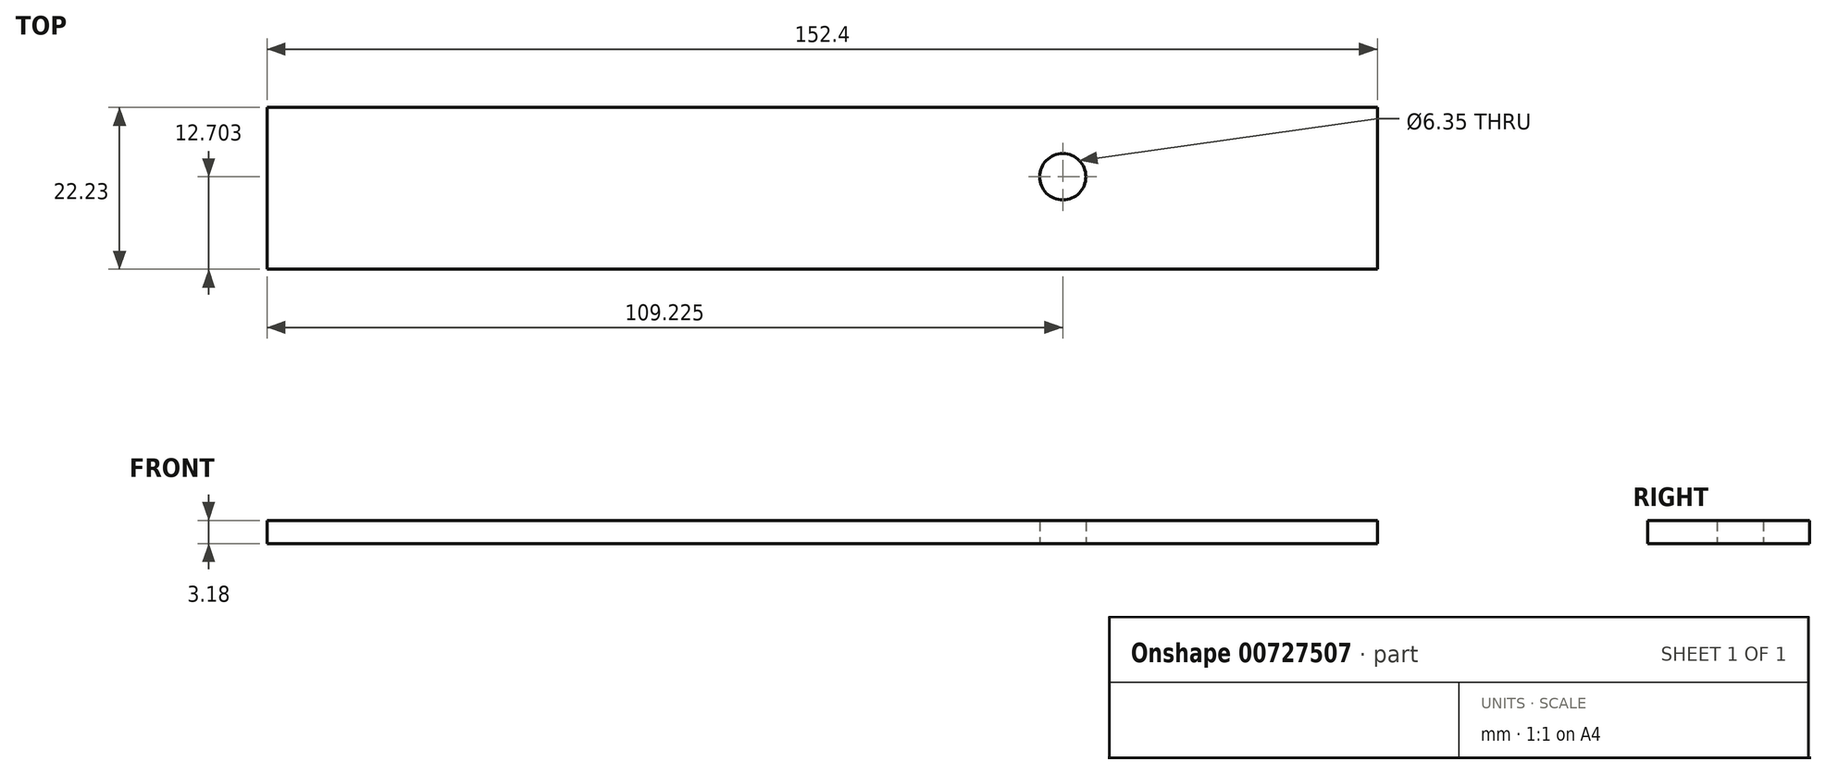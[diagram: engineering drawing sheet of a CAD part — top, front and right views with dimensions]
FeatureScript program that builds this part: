
annotation { "Feature Type Name" : "Feature", "Feature Type Description" : "" }
export const myFeature = defineFeature(function(context is Context, id is Id, definition is map)
    precondition{}
    {
        {
            var Q0;
            Q0=qCreatedBy(makeId("Top.planeOp"),FACE);
            var sketch = newSketch(context, id + "F0", { "sketchPlane" : qUnion([Q0])});
            skLineSegment(sketch, "E0.bottom", {"start": v(-83.24, 4.33) * mm, "end": v(69.16, 4.33) * mm});
            skLineSegment(sketch, "E0.top", {"start": v(-83.24, -17.9) * mm, "end": v(69.16, -17.9) * mm});
            skLineSegment(sketch, "E0.left", {"start": v(-83.24, 4.33) * mm, "end": v(-83.24, -17.9) * mm});
            skLineSegment(sketch, "E0.right", {"start": v(69.16, 4.33) * mm, "end": v(69.16, -17.9) * mm});
            skCircle(sketch, "E1", {"center": v(25.98, -5.2) * mm, "radius": 3.18 * mm});
            skSolve(sketch);
        }
        {
            var Q0;
            Q0 = qSketchRegion(id + "F0", true);
            extrude(context, id + "F1", {"entities" : qUnion([Q0]), "depth" : 3.17 * mm, "offsetDistance" : 25.4 * mm});
        }
    });
